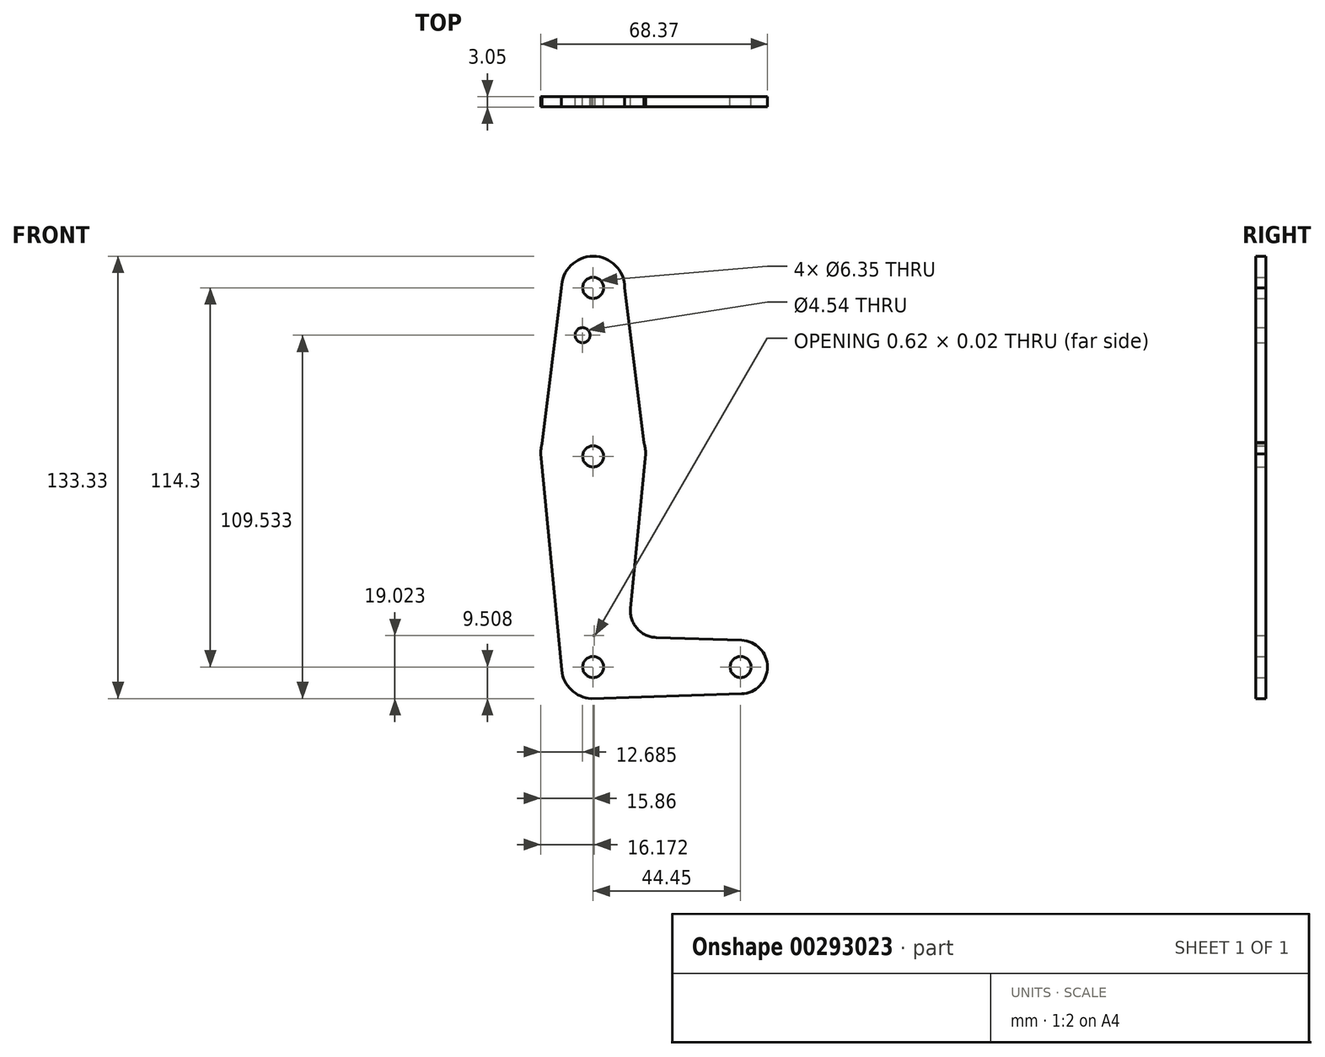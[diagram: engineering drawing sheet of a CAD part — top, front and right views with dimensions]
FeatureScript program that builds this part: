
annotation { "Feature Type Name" : "Feature", "Feature Type Description" : "" }
export const myFeature = defineFeature(function(context is Context, id is Id, definition is map)
    precondition{}
    {
        {
            var Q0;
            Q0=qCreatedBy(makeId("Front.planeOp"),FACE);
            var sketch = newSketch(context, id + "F0", { "sketchPlane" : qUnion([Q0])});
            skCircle(sketch, "E0", {"center": v(-39.46, 85.18) * mm, "radius": 3.18 * mm});
            skCircle(sketch, "E1", {"center": v(-39.46, 85.18) * mm, "radius": 9.53 * mm});
            skCircle(sketch, "E2", {"center": v(-39.46, 34.38) * mm, "radius": 3.18 * mm});
            skCircle(sketch, "E3", {"center": v(-39.46, 34.38) * mm, "radius": 15.88 * mm});
            skCircle(sketch, "E4", {"center": v(-39.46, -29.12) * mm, "radius": 3.18 * mm});
            skCircle(sketch, "E5", {"center": v(-39.46, -29.12) * mm, "radius": 9.52 * mm});
            skCircle(sketch, "E6", {"center": v(5, -29.12) * mm, "radius": 3.18 * mm});
            skCircle(sketch, "E7", {"center": v(5, -29.12) * mm, "radius": 8.06 * mm});
            skLineSegment(sketch, "E8", {"start": v(-48.98, 85.18) * mm, "end": v(-54.88, 38.16) * mm});
            skLineSegment(sketch, "E9", {"start": v(-29.93, 85.18) * mm, "end": v(-24.15, 38.57) * mm});
            skLineSegment(sketch, "E10", {"start": v(-55.32, 35.1) * mm, "end": v(-48.94, -30.05) * mm});
            skLineSegment(sketch, "E11", {"start": v(-23.6, 35.1) * mm, "end": v(-28.16, -11.5) * mm});
            skLineSegment(sketch, "E12", {"start": v(-39.46, -19.6) * mm, "end": v(-38.84, -19.62) * mm});
            skLineSegment(sketch, "E13", {"start": v(-39.98, -38.63) * mm, "end": v(5.25, -37.18) * mm});
            skLineSegment(sketch, "E14.trimOffspring", {"start": v(-20.51, -20.22) * mm, "end": v(5.25, -21.06) * mm});
            skPoint(sketch, "E15.visualSharp", {"position": v(-28.99, -19.94) * mm});
            skArc(sketch, "E15.filletArc", {"start": v(-28.16, -11.5) * mm, "mid": v(-26.23, -17.52) * mm, "end": v(-20.51, -20.22) * mm});
            skCircle(sketch, "E16", {"center": v(-42.63, 70.9) * mm, "radius": 2.27 * mm});
            skSolve(sketch);
        }
        {
            var Q0;
            {var subQ0=sQuery(id+"F0.wireOp",EDGE,"E8");Q0=makeQuery(id+"F0.imprint","IMPRINT",FACE,{"disambiguationData":[TD([[makeQuery(id+"F0.imprint","IMPRINT",EDGE,{"derivedFrom":subQ0}),1.0]])]});}
            var Q1;
            Q1=makeQuery(id+"F0.imprint","IMPRINT",FACE,{"disambiguationData":[TD([[makeQuery(id+"F0.imprint","IMPRINT",EDGE,{"derivedFrom":sQuery(id+"F0.wireOp",EDGE,"E0")}),-1.0]])]});
            var Q2;
            {var subQ14=sQuery(id+"F0.wireOp",EDGE,"E14.trimOffspring");Q2=makeQuery(id+"F0.imprint","IMPRINT",FACE,{"disambiguationData":[TD([[makeQuery(id+"F0.imprint","IMPRINT",EDGE,{"derivedFrom":subQ14}),-1.0]])]});}
            var Q3;
            Q3=makeQuery(id+"F0.imprint","IMPRINT",FACE,{"disambiguationData":[TD([[makeQuery(id+"F0.imprint","IMPRINT",EDGE,{"derivedFrom":sQuery(id+"F0.wireOp",EDGE,"E4")}),-1.0]])]});
            var Q4;
            Q4=makeQuery(id+"F0.imprint","IMPRINT",FACE,{"disambiguationData":[TD([[makeQuery(id+"F0.imprint","IMPRINT",EDGE,{"derivedFrom":sQuery(id+"F0.wireOp",EDGE,"E6")}),-1.0]])]});
            var Q5;
            Q5=makeQuery(id+"F0.imprint","IMPRINT",FACE,{"disambiguationData":[TD([[makeQuery(id+"F0.imprint","IMPRINT",EDGE,{"derivedFrom":sQuery(id+"F0.wireOp",EDGE,"E2")}),-1.0]])]});
            extrude(context, id + "F1", {"entities" : qUnion([Q0, Q1, Q2, Q3, Q4, Q5]), "depth" : 3.05 * mm});
        }
    });
